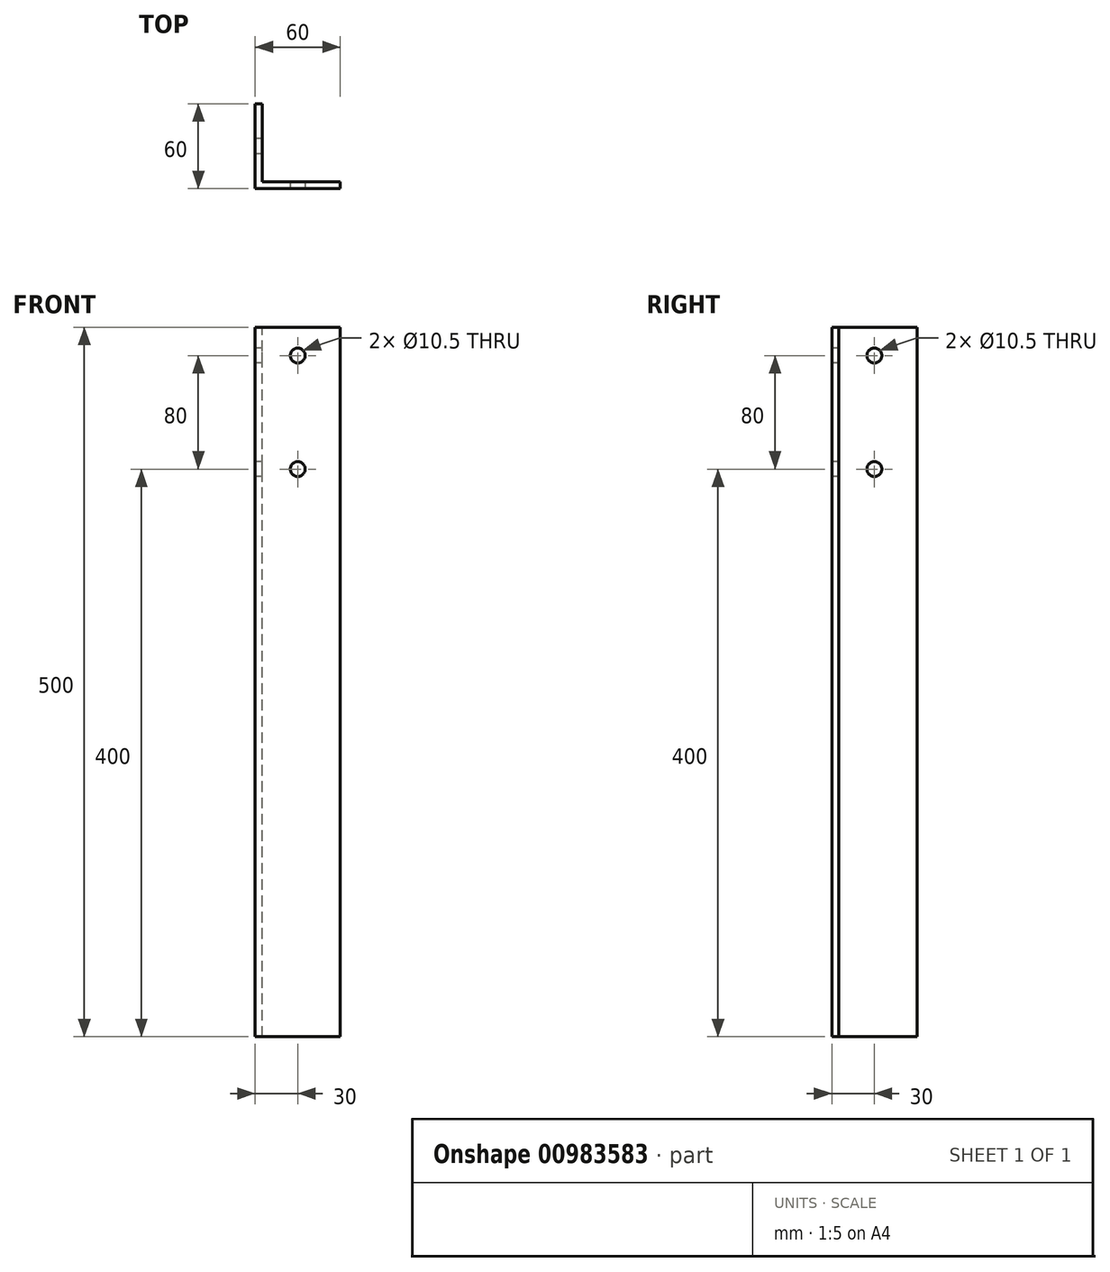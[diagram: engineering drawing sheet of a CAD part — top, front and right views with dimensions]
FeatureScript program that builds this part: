
annotation { "Feature Type Name" : "Feature", "Feature Type Description" : "" }
export const myFeature = defineFeature(function(context is Context, id is Id, definition is map)
    precondition{}
    {
        {
            var Q0;
            Q0=qCreatedBy(makeId("Top.planeOp"),FACE);
            var sketch = newSketch(context, id + "F0", { "sketchPlane" : qUnion([Q0])});
            skLineSegment(sketch, "E0", {"start": v(-30, 30) * mm, "end": v(-30, -30) * mm});
            skLineSegment(sketch, "E1", {"start": v(-30, -30) * mm, "end": v(30, -30) * mm});
            skLineSegment(sketch, "E2", {"start": v(30, -30) * mm, "end": v(30, -25) * mm});
            skLineSegment(sketch, "E3", {"start": v(30, -25) * mm, "end": v(-25, -25) * mm});
            skLineSegment(sketch, "E4", {"start": v(-25, -25) * mm, "end": v(-25, 30) * mm});
            skLineSegment(sketch, "E5", {"start": v(-25, 30) * mm, "end": v(-30, 30) * mm});
            skSolve(sketch);
        }
        {
            var Q0;
            Q0=makeQuery(id+"F0.imprint","IMPRINT",FACE,{"disambiguationData":[TD([[makeQuery(id+"F0.imprint","IMPRINT",EDGE,{"derivedFrom":sQuery(id+"F0.wireOp",EDGE,"E0")}),1.0]])]});
            extrude(context, id + "F1", {"entities" : qUnion([Q0]), "oppositeDirection" : true, "depth" : 500 * mm, "offsetDistance" : 25 * mm});
        }
        {
            var Q0;
            Q0=makeQuery(id+"F1.opExtrude","SWEPT_FACE",FACE,{"disambiguationData":[OSD([sQuery(id+"F0.wireOp",EDGE,"E1")])]});
            var sketch = newSketch(context, id + "F2", { "sketchPlane" : qUnion([Q0])});
            skLineSegment(sketch, "E6", {"start": v(0, 0) * mm, "end": v(0, -83.8) * mm, "construction": true});
            skCircle(sketch, "E7", {"center": v(0, -20) * mm, "radius": 5.25 * mm});
            skCircle(sketch, "E8", {"center": v(0, -100) * mm, "radius": 5.25 * mm});
            skSolve(sketch);
        }
        {
            var Q0;
            Q0=makeQuery(id+"F2.imprint","IMPRINT",FACE,{"disambiguationData":[TD([[makeQuery(id+"F2.imprint","IMPRINT",EDGE,{"derivedFrom":sQuery(id+"F2.wireOp",EDGE,"E7")}),1.0]])]});
            var Q1;
            Q1=makeQuery(id+"F2.imprint","IMPRINT",FACE,{"disambiguationData":[TD([[makeQuery(id+"F2.imprint","IMPRINT",EDGE,{"derivedFrom":sQuery(id+"F2.wireOp",EDGE,"E8")}),1.0]])]});
            extrude(context, id + "F3", {"entities" : qUnion([Q0, Q1]), "operationType" : NewBodyOperationType.REMOVE, "oppositeDirection" : true, "depth" : 10 * mm, "offsetDistance" : 25 * mm});
        }
        {
            var Q0;
            Q0=makeQuery(id+"F1.opExtrude","SWEPT_FACE",FACE,{"disambiguationData":[OSD([sQuery(id+"F0.wireOp",EDGE,"E0")])]});
            var sketch = newSketch(context, id + "F4", { "sketchPlane" : qUnion([Q0])});
            skLineSegment(sketch, "E9", {"start": v(0, 0) * mm, "end": v(0, -162.83) * mm, "construction": true});
            skCircle(sketch, "E10", {"center": v(0, -20) * mm, "radius": 5.25 * mm});
            skCircle(sketch, "E11", {"center": v(0, -100) * mm, "radius": 5.25 * mm});
            skSolve(sketch);
        }
        {
            var Q0;
            Q0=makeQuery(id+"F4.imprint","IMPRINT",FACE,{"disambiguationData":[TD([[makeQuery(id+"F4.imprint","IMPRINT",EDGE,{"derivedFrom":sQuery(id+"F4.wireOp",EDGE,"E10")}),1.0]])]});
            var Q1;
            Q1=makeQuery(id+"F4.imprint","IMPRINT",FACE,{"disambiguationData":[TD([[makeQuery(id+"F4.imprint","IMPRINT",EDGE,{"derivedFrom":sQuery(id+"F4.wireOp",EDGE,"E11")}),1.0]])]});
            extrude(context, id + "F5", {"entities" : qUnion([Q0, Q1]), "operationType" : NewBodyOperationType.REMOVE, "oppositeDirection" : true, "depth" : 10 * mm, "offsetDistance" : 25 * mm});
        }
    });
